# Revit family: Basin-Undermount-Sloan-(SS-3002_SS-3102_SS-3802)_Series
name_source: partatom
category: Plumbing Fixtures
revit_build: Autodesk Revit 2014 (Build: 20130308_1515(x64)
units: mm (PartAtom-declared; Revit-internal decimal feet)

## types (5) — shared parameters
ADA Compliant = Yes
Assembly Code = D2010440
CW Connection = Yes
CWFU = 1.5
Cold Water Connection Diameter = 3/8"
Cold Water Connection Height = 11"
Cold Water Connection Radius = 3/16"
Cold Water Connection Width = 4"
Default Elevation = 34"
HW Connection = Yes
HWFU = 1.5
Height = 34"
Hot Water Connection Diameter = 0"
Hot Water Connection Height = 11"
Hot Water Connection Radius = 3/16"
Hot Water Connection Width = 4"
Length = 34"
Manufacturer = Sloan
Material = Vitreous China-Sloan-White
Product Page URL = https://www.sloan.com
Revised Date = 8/10/2015
URL = http://www.sloan.com
Vent Connection = No
WFU = 2
Waste Connection = Yes
Waste Connection Diameter = 1 1/4"
Waste Connection Height = 12 3/4"
Waste Connection Radius = 5/8"
Width = 20"

## per-type parameters (varying)
| type | Description | Hole Distance | Hole Visibility | Order Code | Product Documentation Link |
| SS-3002 | Complete vitreous china lavatory. SS-3002 Basin, 4" (102mm) centers holes, 20" x 17" x 7-1/2" (508mm x 431mm x 191mm) deep, counter mounted, vitreous china, front overflow, self rimming. | 4" | Yes | 3873002 | https://specifications.sloan.com |
| SS-3002-STG | 20"x17" Drop-in Oval Lav-4"CS w/ SloanTec Glaze | 4" | Yes | 3873072 | https://specifications.sloan.com |
| SS-3102 | SS-3102 Basin, center hole only, 20" x 17" x 7-1/2" (508mm x 431mm x 191mm) deep, counter mounted, vitreous china, front overflow, self rimming. | 30" | No | 3873102 | https://specifications.sloan.com |
| SS-3102-STG | SS-3102 Basin, center hole only, 20" x 17" x 7-1/2" (508mm x 431mm x 191mm) deep, counter mounted, vitreous china, front overflow, self rimming. | 30" | No | 3873172 | https://specifications.sloan.com |
| SS-3802 | Complete vitreous china lavatory. SS-3802 Basin, 8" (203mm) centerset holes, 20" x 17" x 7-1/2" (508mm x 431mm x 191mm) deep, counter mounted, vitreous china, front overflow, self rimming. | 8" | Yes | 3873802 |  |

note: column(s) folded — value = type name in every type: Model

## geometry (parser evidence)
native form markers: Sweep x1
no freeform markers — native parametric forms only
